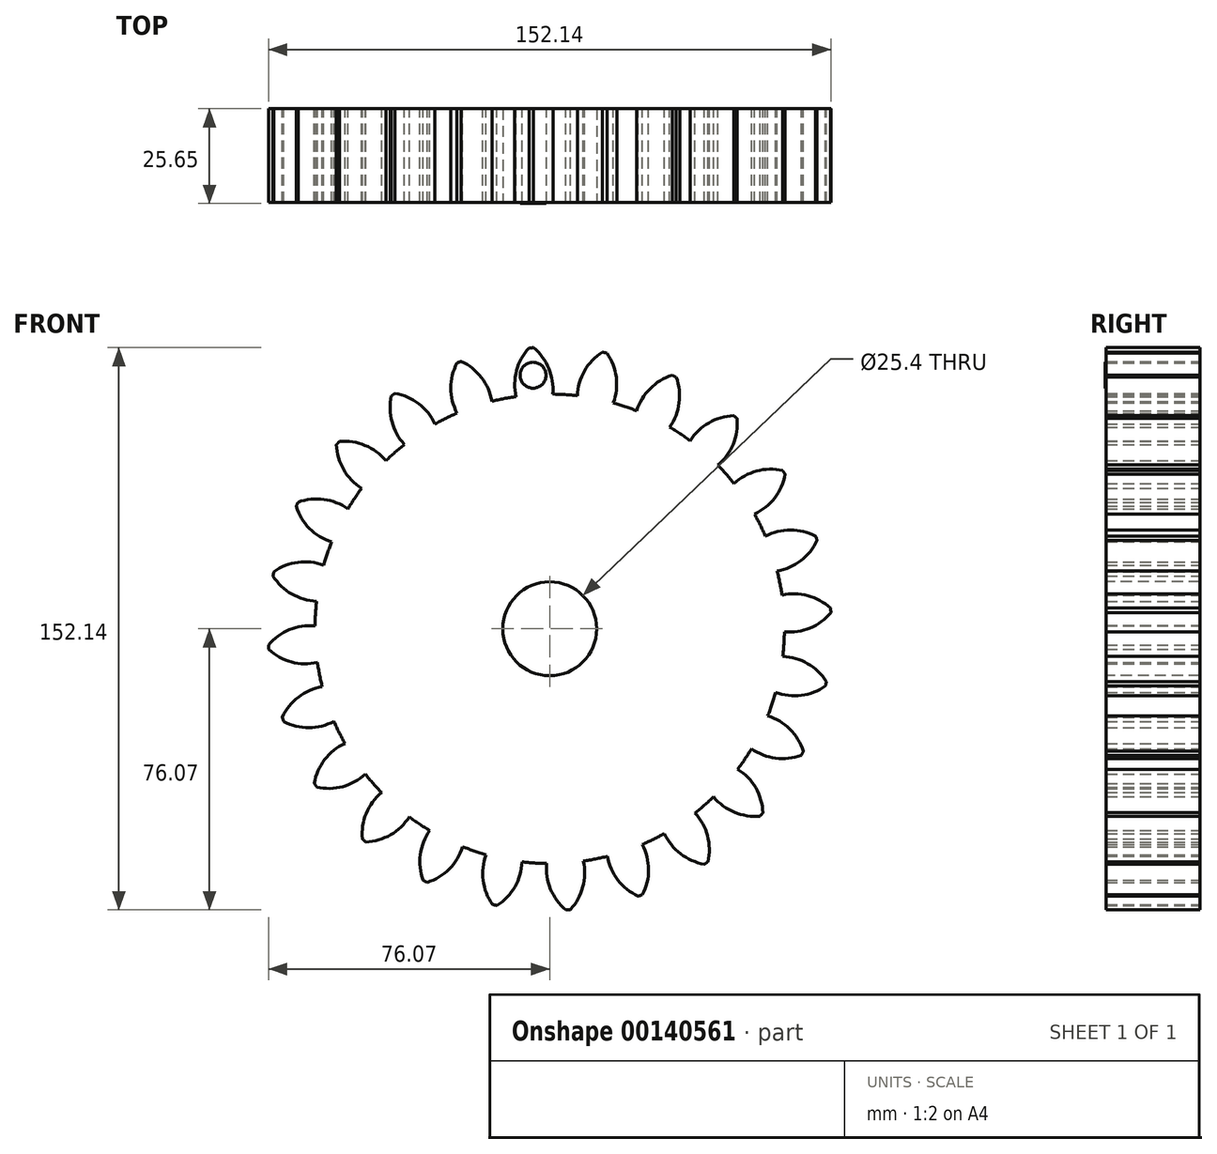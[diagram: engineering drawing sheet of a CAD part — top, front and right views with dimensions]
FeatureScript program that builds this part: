
annotation { "Feature Type Name" : "Feature", "Feature Type Description" : "" }
export const myFeature = defineFeature(function(context is Context, id is Id, definition is map)
    precondition{}
    {
        {
            var Q0;
            Q0=qCreatedBy(makeId("Front.planeOp"),FACE);
            var sketch = newSketch(context, id + "F0", { "sketchPlane" : qUnion([Q0])});
            skPoint(sketch, "E0.rect.middle", {"position": v(0, 0) * mm});
            skLineSegment(sketch, "E1", {"start": v(0, 0) * mm, "end": v(0, 76.2) * mm});
            skLineSegment(sketch, "E2", {"start": v(0, 0) * mm, "end": v(0, -76.2) * mm});
            skLineSegment(sketch, "E3", {"start": v(0, 0) * mm, "end": v(19.72, 73.6) * mm});
            skLineSegment(sketch, "E4", {"start": v(0, 0) * mm, "end": v(38.1, 66) * mm});
            skLineSegment(sketch, "E5", {"start": v(0, 0) * mm, "end": v(53.88, 53.88) * mm});
            skLineSegment(sketch, "E6", {"start": v(0, 0) * mm, "end": v(66, 38.1) * mm});
            skLineSegment(sketch, "E7", {"start": v(0, 0) * mm, "end": v(73.6, 19.72) * mm});
            skLineSegment(sketch, "E8", {"start": v(0, 0) * mm, "end": v(76.2, 0) * mm});
            skLineSegment(sketch, "E9", {"start": v(0, 0) * mm, "end": v(73.6, -19.72) * mm});
            skLineSegment(sketch, "E10", {"start": v(0, 0) * mm, "end": v(66, -38.1) * mm});
            skLineSegment(sketch, "E11", {"start": v(0, 0) * mm, "end": v(53.88, -53.88) * mm});
            skLineSegment(sketch, "E12", {"start": v(0, 0) * mm, "end": v(38.1, -66) * mm});
            skLineSegment(sketch, "E13", {"start": v(0, 0) * mm, "end": v(19.72, -73.6) * mm});
            skLineSegment(sketch, "E14", {"start": v(0, 0) * mm, "end": v(-19.72, -73.6) * mm});
            skLineSegment(sketch, "E15", {"start": v(0, 0) * mm, "end": v(-38.1, -66) * mm});
            skLineSegment(sketch, "E16", {"start": v(0, 0) * mm, "end": v(-53.88, -53.88) * mm});
            skLineSegment(sketch, "E17", {"start": v(0, 0) * mm, "end": v(-66, -38.1) * mm});
            skLineSegment(sketch, "E18", {"start": v(0, 0) * mm, "end": v(-73.6, -19.72) * mm});
            skLineSegment(sketch, "E19", {"start": v(0, 0) * mm, "end": v(-76.2, 0.07) * mm});
            skLineSegment(sketch, "E20", {"start": v(0, 0) * mm, "end": v(-73.6, 19.72) * mm});
            skLineSegment(sketch, "E21", {"start": v(0, 0) * mm, "end": v(-66, 38.1) * mm});
            skLineSegment(sketch, "E22", {"start": v(0, 0) * mm, "end": v(-53.88, 53.88) * mm});
            skLineSegment(sketch, "E23", {"start": v(0, 0) * mm, "end": v(-38.1, 66) * mm});
            skLineSegment(sketch, "E24", {"start": v(0, 0) * mm, "end": v(-19.72, 73.6) * mm});
            skCircle(sketch, "E25", {"center": v(0, 0) * mm, "radius": 76.2 * mm});
            skCircle(sketch, "E26", {"center": v(0, 0) * mm, "radius": 69.85 * mm});
            skCircle(sketch, "E27", {"center": v(0, 0) * mm, "radius": 63.5 * mm});
            skLineSegment(sketch, "E28", {"start": v(0, 0) * mm, "end": v(-4.98, 76.04) * mm});
            skLineSegment(sketch, "E29", {"start": v(0, 69.85) * mm, "end": v(-76.58, 69.85) * mm});
            skLineSegment(sketch, "E30", {"start": v(0, 69.85) * mm, "end": v(-76.5, 42) * mm});
            skLineSegment(sketch, "E31", {"start": v(-4.98, 76.04) * mm, "end": v(-7.15, 109.16) * mm});
            skLineSegment(sketch, "E32", {"start": v(0, 76.2) * mm, "end": v(0, 110.22) * mm});
            skCircle(sketch, "E33", {"center": v(0, 69.85) * mm, "radius": 14.6 * mm});
            skPoint(sketch, "E34", {"position": v(-13.72, 64.85) * mm});
            skArc(sketch, "E35", {"start": v(0.82, 63.5) * mm, "mid": v(-0.22, 70.43) * mm, "end": v(-4.37, 76.07) * mm});
            skArc(sketch, "E36.MirrorCS", {"start": v(-9.1, 62.84) * mm, "mid": v(-8.97, 69.85) * mm, "end": v(-5.6, 76) * mm});
            skSolve(sketch);
        }
        {
            var Q0;
            {var subQ1=sQuery(id+"F0.wireOp",EDGE,"E23");var subQ3=sQuery(id+"F0.wireOp",EDGE,"E27");var subQ4=makeQuery(id+"F0.imprint","INTERSECT",VERTEX,{"derivedFrom":[subQ1,subQ3]});Q0=makeQuery(id+"F0.imprint","IMPRINT",FACE,{"disambiguationData":[TD([[makeQuery(id+"F0.imprint","IMPRINT",EDGE,{"disambiguationData":[TD([[subQ4,1.0]])],"derivedFrom":subQ3}),1.0]])]});}
            var Q1;
            {var subQ1=sQuery(id+"F0.wireOp",EDGE,"E22");var subQ3=sQuery(id+"F0.wireOp",EDGE,"E27");var subQ4=makeQuery(id+"F0.imprint","INTERSECT",VERTEX,{"derivedFrom":[subQ1,subQ3]});Q1=makeQuery(id+"F0.imprint","IMPRINT",FACE,{"disambiguationData":[TD([[makeQuery(id+"F0.imprint","IMPRINT",EDGE,{"disambiguationData":[TD([[subQ4,1.0]])],"derivedFrom":subQ3}),1.0]])]});}
            var Q2;
            {var subQ1=sQuery(id+"F0.wireOp",EDGE,"E1");var subQ3=sQuery(id+"F0.wireOp",EDGE,"E33");var subQ4=makeQuery(id+"F0.imprint","INTERSECT",VERTEX,{"derivedFrom":[subQ1,subQ3]});Q2=makeQuery(id+"F0.imprint","IMPRINT",FACE,{"disambiguationData":[TD([[makeQuery(id+"F0.imprint","IMPRINT",EDGE,{"disambiguationData":[TD([[subQ4,1.0]])],"derivedFrom":subQ3}),-1.0]])]});}
            var Q3;
            {var subQ1=sQuery(id+"F0.wireOp",EDGE,"E19");var subQ3=sQuery(id+"F0.wireOp",EDGE,"E27");var subQ4=makeQuery(id+"F0.imprint","INTERSECT",VERTEX,{"derivedFrom":[subQ1,subQ3]});Q3=makeQuery(id+"F0.imprint","IMPRINT",FACE,{"disambiguationData":[TD([[makeQuery(id+"F0.imprint","IMPRINT",EDGE,{"disambiguationData":[TD([[subQ4,1.0]])],"derivedFrom":subQ3}),1.0]])]});}
            var Q4;
            {var subQ1=sQuery(id+"F0.wireOp",EDGE,"E24");var subQ3=sQuery(id+"F0.wireOp",EDGE,"E27");var subQ4=makeQuery(id+"F0.imprint","INTERSECT",VERTEX,{"derivedFrom":[subQ1,subQ3]});Q4=makeQuery(id+"F0.imprint","IMPRINT",FACE,{"disambiguationData":[TD([[makeQuery(id+"F0.imprint","IMPRINT",EDGE,{"disambiguationData":[TD([[subQ4,1.0]])],"derivedFrom":subQ3}),1.0]])]});}
            var Q5;
            {var subQ1=sQuery(id+"F0.wireOp",EDGE,"E20");var subQ3=sQuery(id+"F0.wireOp",EDGE,"E27");var subQ4=makeQuery(id+"F0.imprint","INTERSECT",VERTEX,{"derivedFrom":[subQ1,subQ3]});Q5=makeQuery(id+"F0.imprint","IMPRINT",FACE,{"disambiguationData":[TD([[makeQuery(id+"F0.imprint","IMPRINT",EDGE,{"disambiguationData":[TD([[subQ4,1.0]])],"derivedFrom":subQ3}),1.0]])]});}
            var Q6;
            {var subQ1=sQuery(id+"F0.wireOp",EDGE,"E21");var subQ3=sQuery(id+"F0.wireOp",EDGE,"E27");var subQ4=makeQuery(id+"F0.imprint","INTERSECT",VERTEX,{"derivedFrom":[subQ1,subQ3]});Q6=makeQuery(id+"F0.imprint","IMPRINT",FACE,{"disambiguationData":[TD([[makeQuery(id+"F0.imprint","IMPRINT",EDGE,{"disambiguationData":[TD([[subQ4,1.0]])],"derivedFrom":subQ3}),1.0]])]});}
            var Q7;
            {var subQ1=sQuery(id+"F0.wireOp",EDGE,"E6");var subQ3=sQuery(id+"F0.wireOp",EDGE,"E27");var subQ4=makeQuery(id+"F0.imprint","INTERSECT",VERTEX,{"derivedFrom":[subQ1,subQ3]});Q7=makeQuery(id+"F0.imprint","IMPRINT",FACE,{"disambiguationData":[TD([[makeQuery(id+"F0.imprint","IMPRINT",EDGE,{"disambiguationData":[TD([[subQ4,1.0]])],"derivedFrom":subQ3}),1.0]])]});}
            var Q8;
            {var subQ1=sQuery(id+"F0.wireOp",EDGE,"E4");var subQ3=sQuery(id+"F0.wireOp",EDGE,"E27");var subQ4=makeQuery(id+"F0.imprint","INTERSECT",VERTEX,{"derivedFrom":[subQ1,subQ3]});Q8=makeQuery(id+"F0.imprint","IMPRINT",FACE,{"disambiguationData":[TD([[makeQuery(id+"F0.imprint","IMPRINT",EDGE,{"disambiguationData":[TD([[subQ4,1.0]])],"derivedFrom":subQ3}),1.0]])]});}
            var Q9;
            {var subQ1=sQuery(id+"F0.wireOp",EDGE,"E7");var subQ3=sQuery(id+"F0.wireOp",EDGE,"E27");var subQ4=makeQuery(id+"F0.imprint","INTERSECT",VERTEX,{"derivedFrom":[subQ1,subQ3]});Q9=makeQuery(id+"F0.imprint","IMPRINT",FACE,{"disambiguationData":[TD([[makeQuery(id+"F0.imprint","IMPRINT",EDGE,{"disambiguationData":[TD([[subQ4,1.0]])],"derivedFrom":subQ3}),1.0]])]});}
            var Q10;
            {var subQ0=sQuery(id+"F0.wireOp",EDGE,"E3");var subQ5=sQuery(id+"F0.wireOp",EDGE,"E27");var subQ6=makeQuery(id+"F0.imprint","INTERSECT",VERTEX,{"derivedFrom":[subQ0,subQ5]});Q10=makeQuery(id+"F0.imprint","IMPRINT",FACE,{"disambiguationData":[TD([[makeQuery(id+"F0.imprint","IMPRINT",EDGE,{"disambiguationData":[TD([[subQ6,-1.0]])],"derivedFrom":subQ5}),1.0]])]});}
            var Q11;
            {var subQ1=sQuery(id+"F0.wireOp",EDGE,"E3");var subQ3=sQuery(id+"F0.wireOp",EDGE,"E27");var subQ4=makeQuery(id+"F0.imprint","INTERSECT",VERTEX,{"derivedFrom":[subQ1,subQ3]});Q11=makeQuery(id+"F0.imprint","IMPRINT",FACE,{"disambiguationData":[TD([[makeQuery(id+"F0.imprint","IMPRINT",EDGE,{"disambiguationData":[TD([[subQ4,1.0]])],"derivedFrom":subQ3}),1.0]])]});}
            var Q12;
            {var subQ1=sQuery(id+"F0.wireOp",EDGE,"E5");var subQ3=sQuery(id+"F0.wireOp",EDGE,"E27");var subQ4=makeQuery(id+"F0.imprint","INTERSECT",VERTEX,{"derivedFrom":[subQ1,subQ3]});Q12=makeQuery(id+"F0.imprint","IMPRINT",FACE,{"disambiguationData":[TD([[makeQuery(id+"F0.imprint","IMPRINT",EDGE,{"disambiguationData":[TD([[subQ4,1.0]])],"derivedFrom":subQ3}),1.0]])]});}
            var Q13;
            {var subQ1=sQuery(id+"F0.wireOp",EDGE,"E17");var subQ3=sQuery(id+"F0.wireOp",EDGE,"E27");var subQ4=makeQuery(id+"F0.imprint","INTERSECT",VERTEX,{"derivedFrom":[subQ1,subQ3]});Q13=makeQuery(id+"F0.imprint","IMPRINT",FACE,{"disambiguationData":[TD([[makeQuery(id+"F0.imprint","IMPRINT",EDGE,{"disambiguationData":[TD([[subQ4,1.0]])],"derivedFrom":subQ3}),1.0]])]});}
            var Q14;
            {var subQ1=sQuery(id+"F0.wireOp",EDGE,"E15");var subQ3=sQuery(id+"F0.wireOp",EDGE,"E27");var subQ4=makeQuery(id+"F0.imprint","INTERSECT",VERTEX,{"derivedFrom":[subQ1,subQ3]});Q14=makeQuery(id+"F0.imprint","IMPRINT",FACE,{"disambiguationData":[TD([[makeQuery(id+"F0.imprint","IMPRINT",EDGE,{"disambiguationData":[TD([[subQ4,1.0]])],"derivedFrom":subQ3}),1.0]])]});}
            var Q15;
            {var subQ1=sQuery(id+"F0.wireOp",EDGE,"E16");var subQ3=sQuery(id+"F0.wireOp",EDGE,"E27");var subQ4=makeQuery(id+"F0.imprint","INTERSECT",VERTEX,{"derivedFrom":[subQ1,subQ3]});Q15=makeQuery(id+"F0.imprint","IMPRINT",FACE,{"disambiguationData":[TD([[makeQuery(id+"F0.imprint","IMPRINT",EDGE,{"disambiguationData":[TD([[subQ4,1.0]])],"derivedFrom":subQ3}),1.0]])]});}
            var Q16;
            {var subQ1=sQuery(id+"F0.wireOp",EDGE,"E2");var subQ3=sQuery(id+"F0.wireOp",EDGE,"E27");var subQ4=makeQuery(id+"F0.imprint","INTERSECT",VERTEX,{"derivedFrom":[subQ1,subQ3]});Q16=makeQuery(id+"F0.imprint","IMPRINT",FACE,{"disambiguationData":[TD([[makeQuery(id+"F0.imprint","IMPRINT",EDGE,{"disambiguationData":[TD([[subQ4,1.0]])],"derivedFrom":subQ3}),1.0]])]});}
            var Q17;
            {var subQ1=sQuery(id+"F0.wireOp",EDGE,"E14");var subQ3=sQuery(id+"F0.wireOp",EDGE,"E27");var subQ4=makeQuery(id+"F0.imprint","INTERSECT",VERTEX,{"derivedFrom":[subQ1,subQ3]});Q17=makeQuery(id+"F0.imprint","IMPRINT",FACE,{"disambiguationData":[TD([[makeQuery(id+"F0.imprint","IMPRINT",EDGE,{"disambiguationData":[TD([[subQ4,1.0]])],"derivedFrom":subQ3}),1.0]])]});}
            var Q18;
            {var subQ1=sQuery(id+"F0.wireOp",EDGE,"E18");var subQ3=sQuery(id+"F0.wireOp",EDGE,"E27");var subQ4=makeQuery(id+"F0.imprint","INTERSECT",VERTEX,{"derivedFrom":[subQ1,subQ3]});Q18=makeQuery(id+"F0.imprint","IMPRINT",FACE,{"disambiguationData":[TD([[makeQuery(id+"F0.imprint","IMPRINT",EDGE,{"disambiguationData":[TD([[subQ4,1.0]])],"derivedFrom":subQ3}),1.0]])]});}
            var Q19;
            {var subQ0=sQuery(id+"F0.wireOp",EDGE,"E33");var subQ1=sQuery(id+"F0.wireOp",EDGE,"E1");var subQ2=makeQuery(id+"F0.imprint","INTERSECT",VERTEX,{"derivedFrom":[subQ1,subQ0]});Q19=makeQuery(id+"F0.imprint","IMPRINT",FACE,{"disambiguationData":[TD([[makeQuery(id+"F0.imprint","IMPRINT",EDGE,{"disambiguationData":[TD([[subQ2,-1.0]])],"derivedFrom":subQ1}),1.0]])]});}
            var Q20;
            {var subQ0=sQuery(id+"F0.wireOp",EDGE,"E27");var subQ1=makeQuery(id+"F0.imprint","INTERSECT",VERTEX,{"derivedFrom":[subQ0,sQuery(id+"F0.wireOp",EDGE,"E36.MirrorCS")]});Q20=makeQuery(id+"F0.imprint","IMPRINT",FACE,{"disambiguationData":[TD([[makeQuery(id+"F0.imprint","IMPRINT",EDGE,{"disambiguationData":[TD([[subQ1,1.0]])],"derivedFrom":subQ0}),1.0]])]});}
            var Q21;
            {var subQ0=sQuery(id+"F0.wireOp",EDGE,"E33");var subQ1=sQuery(id+"F0.wireOp",EDGE,"E1");var subQ2=makeQuery(id+"F0.imprint","INTERSECT",VERTEX,{"derivedFrom":[subQ1,subQ0]});Q21=makeQuery(id+"F0.imprint","IMPRINT",FACE,{"disambiguationData":[TD([[makeQuery(id+"F0.imprint","IMPRINT",EDGE,{"disambiguationData":[TD([[subQ2,-1.0]])],"derivedFrom":subQ1}),-1.0]])]});}
            var Q22;
            {var subQ1=sQuery(id+"F0.wireOp",EDGE,"E1");var subQ3=sQuery(id+"F0.wireOp",EDGE,"E27");var subQ4=makeQuery(id+"F0.imprint","INTERSECT",VERTEX,{"derivedFrom":[subQ1,subQ3]});Q22=makeQuery(id+"F0.imprint","IMPRINT",FACE,{"disambiguationData":[TD([[makeQuery(id+"F0.imprint","IMPRINT",EDGE,{"disambiguationData":[TD([[subQ4,-1.0]])],"derivedFrom":subQ3}),-1.0]])]});}
            var Q23;
            {var subQ0=sQuery(id+"F0.wireOp",EDGE,"E36.MirrorCS");var subQ1=sQuery(id+"F0.wireOp",EDGE,"E27");var subQ2=makeQuery(id+"F0.imprint","INTERSECT",VERTEX,{"derivedFrom":[subQ1,subQ0]});Q23=makeQuery(id+"F0.imprint","IMPRINT",FACE,{"disambiguationData":[TD([[makeQuery(id+"F0.imprint","IMPRINT",EDGE,{"disambiguationData":[TD([[subQ2,1.0]])],"derivedFrom":subQ1}),-1.0]])]});}
            var Q24;
            {var subQ0=sQuery(id+"F0.wireOp",EDGE,"E28");var subQ1=sQuery(id+"F0.wireOp",EDGE,"E26");var subQ2=makeQuery(id+"F0.imprint","INTERSECT",VERTEX,{"derivedFrom":[subQ1,subQ0]});Q24=makeQuery(id+"F0.imprint","IMPRINT",FACE,{"disambiguationData":[TD([[makeQuery(id+"F0.imprint","IMPRINT",EDGE,{"disambiguationData":[TD([[subQ2,-1.0]])],"derivedFrom":subQ1}),1.0]])]});}
            var Q25;
            {var subQ0=sQuery(id+"F0.wireOp",EDGE,"E28");var subQ1=sQuery(id+"F0.wireOp",EDGE,"E26");var subQ2=makeQuery(id+"F0.imprint","INTERSECT",VERTEX,{"derivedFrom":[subQ1,subQ0]});Q25=makeQuery(id+"F0.imprint","IMPRINT",FACE,{"disambiguationData":[TD([[makeQuery(id+"F0.imprint","IMPRINT",EDGE,{"disambiguationData":[TD([[subQ2,-1.0]])],"derivedFrom":subQ1}),-1.0]])]});}
            var Q26;
            {var subQ0=sQuery(id+"F0.wireOp",EDGE,"E28");var subQ5=sQuery(id+"F0.wireOp",EDGE,"E29");var subQ6=makeQuery(id+"F0.imprint","INTERSECT",VERTEX,{"derivedFrom":[subQ0,subQ5]});Q26=makeQuery(id+"F0.imprint","IMPRINT",FACE,{"disambiguationData":[TD([[makeQuery(id+"F0.imprint","IMPRINT",EDGE,{"disambiguationData":[TD([[subQ6,-1.0]])],"derivedFrom":subQ5}),-1.0]])]});}
            var Q27;
            {var subQ1=sQuery(id+"F0.wireOp",EDGE,"E25");var subQ3=sQuery(id+"F0.wireOp",EDGE,"E35");var subQ4=makeQuery(id+"F0.imprint","INTERSECT",VERTEX,{"derivedFrom":[subQ1,subQ3]});Q27=makeQuery(id+"F0.imprint","IMPRINT",FACE,{"disambiguationData":[TD([[makeQuery(id+"F0.imprint","IMPRINT",EDGE,{"disambiguationData":[TD([[subQ4,-1.0]])],"derivedFrom":subQ1}),1.0]])]});}
            var Q28;
            {var subQ0=sQuery(id+"F0.wireOp",EDGE,"E35");var subQ3=sQuery(id+"F0.wireOp",EDGE,"E27");var subQ5=makeQuery(id+"F0.imprint","INTERSECT",VERTEX,{"derivedFrom":[subQ3,subQ0]});Q28=makeQuery(id+"F0.imprint","IMPRINT",FACE,{"disambiguationData":[TD([[makeQuery(id+"F0.imprint","IMPRINT",EDGE,{"disambiguationData":[TD([[subQ5,-1.0]])],"derivedFrom":subQ3}),-1.0]])]});}
            var Q29;
            {var subQ1=sQuery(id+"F0.wireOp",EDGE,"E26");var subQ3=sQuery(id+"F0.wireOp",EDGE,"E28");var subQ4=makeQuery(id+"F0.imprint","INTERSECT",VERTEX,{"derivedFrom":[subQ1,subQ3]});Q29=makeQuery(id+"F0.imprint","IMPRINT",FACE,{"disambiguationData":[TD([[makeQuery(id+"F0.imprint","IMPRINT",EDGE,{"disambiguationData":[TD([[subQ4,-1.0]])],"derivedFrom":subQ3}),-1.0]])]});}
            var Q30;
            {var subQ1=sQuery(id+"F0.wireOp",EDGE,"E26");var subQ3=sQuery(id+"F0.wireOp",EDGE,"E28");var subQ4=makeQuery(id+"F0.imprint","INTERSECT",VERTEX,{"derivedFrom":[subQ1,subQ3]});Q30=makeQuery(id+"F0.imprint","IMPRINT",FACE,{"disambiguationData":[TD([[makeQuery(id+"F0.imprint","IMPRINT",EDGE,{"disambiguationData":[TD([[subQ4,1.0]])],"derivedFrom":subQ3}),-1.0]])]});}
            var Q31;
            {var subQ1=sQuery(id+"F0.wireOp",EDGE,"E10");var subQ3=sQuery(id+"F0.wireOp",EDGE,"E27");var subQ4=makeQuery(id+"F0.imprint","INTERSECT",VERTEX,{"derivedFrom":[subQ1,subQ3]});Q31=makeQuery(id+"F0.imprint","IMPRINT",FACE,{"disambiguationData":[TD([[makeQuery(id+"F0.imprint","IMPRINT",EDGE,{"disambiguationData":[TD([[subQ4,1.0]])],"derivedFrom":subQ3}),1.0]])]});}
            var Q32;
            {var subQ1=sQuery(id+"F0.wireOp",EDGE,"E9");var subQ3=sQuery(id+"F0.wireOp",EDGE,"E27");var subQ4=makeQuery(id+"F0.imprint","INTERSECT",VERTEX,{"derivedFrom":[subQ1,subQ3]});Q32=makeQuery(id+"F0.imprint","IMPRINT",FACE,{"disambiguationData":[TD([[makeQuery(id+"F0.imprint","IMPRINT",EDGE,{"disambiguationData":[TD([[subQ4,1.0]])],"derivedFrom":subQ3}),1.0]])]});}
            var Q33;
            {var subQ1=sQuery(id+"F0.wireOp",EDGE,"E8");var subQ3=sQuery(id+"F0.wireOp",EDGE,"E27");var subQ4=makeQuery(id+"F0.imprint","INTERSECT",VERTEX,{"derivedFrom":[subQ1,subQ3]});Q33=makeQuery(id+"F0.imprint","IMPRINT",FACE,{"disambiguationData":[TD([[makeQuery(id+"F0.imprint","IMPRINT",EDGE,{"disambiguationData":[TD([[subQ4,1.0]])],"derivedFrom":subQ3}),1.0]])]});}
            var Q34;
            {var subQ1=sQuery(id+"F0.wireOp",EDGE,"E11");var subQ3=sQuery(id+"F0.wireOp",EDGE,"E27");var subQ4=makeQuery(id+"F0.imprint","INTERSECT",VERTEX,{"derivedFrom":[subQ1,subQ3]});Q34=makeQuery(id+"F0.imprint","IMPRINT",FACE,{"disambiguationData":[TD([[makeQuery(id+"F0.imprint","IMPRINT",EDGE,{"disambiguationData":[TD([[subQ4,1.0]])],"derivedFrom":subQ3}),1.0]])]});}
            var Q35;
            {var subQ1=sQuery(id+"F0.wireOp",EDGE,"E2");var subQ3=sQuery(id+"F0.wireOp",EDGE,"E27");var subQ4=makeQuery(id+"F0.imprint","INTERSECT",VERTEX,{"derivedFrom":[subQ1,subQ3]});Q35=makeQuery(id+"F0.imprint","IMPRINT",FACE,{"disambiguationData":[TD([[makeQuery(id+"F0.imprint","IMPRINT",EDGE,{"disambiguationData":[TD([[subQ4,-1.0]])],"derivedFrom":subQ3}),1.0]])]});}
            var Q36;
            {var subQ1=sQuery(id+"F0.wireOp",EDGE,"E12");var subQ3=sQuery(id+"F0.wireOp",EDGE,"E27");var subQ4=makeQuery(id+"F0.imprint","INTERSECT",VERTEX,{"derivedFrom":[subQ1,subQ3]});Q36=makeQuery(id+"F0.imprint","IMPRINT",FACE,{"disambiguationData":[TD([[makeQuery(id+"F0.imprint","IMPRINT",EDGE,{"disambiguationData":[TD([[subQ4,1.0]])],"derivedFrom":subQ3}),1.0]])]});}
            extrude(context, id + "F1", {"entities" : qUnion([Q0, Q1, Q2, Q3, Q4, Q5, Q6, Q7, Q8, Q9, Q10, Q11, Q12, Q13, Q14, Q15, Q16, Q17, Q18, Q19, Q20, Q21, Q22, Q23, Q24, Q25, Q26, Q27, Q28, Q29, Q30, Q31, Q32, Q33, Q34, Q35, Q36]), "endBound" : BoundingType.SYMMETRIC, "depth" : 25.4 * mm});
        }
        {
            var Q0;
            Q0=makeQuery(id+"F1.opExtrude","SWEPT_BODY",BODY,{"disambiguationData":[OSD([sQuery(id+"F0.wireOp",EDGE,"E25"),sQuery(id+"F0.wireOp",EDGE,"E27"),sQuery(id+"F0.wireOp",EDGE,"E35"),sQuery(id+"F0.wireOp",EDGE,"E36.MirrorCS")])]});
            var Q1;
            Q1=makeQuery(id+"F1.opExtrude","SWEPT_FACE",FACE,{"disambiguationData":[OSD([sQuery(id+"F0.wireOp",EDGE,"E27")])]});
            circularPattern(context, id + "F2", {"operationType" : NewBodyOperationType.ADD, "entities" : qUnion([Q0]), "axis" : qUnion([Q1]), "angle" : 15 * degree, "instanceCount" : 24});
        }
        {
            var Q0;
            Q0=makeQuery(id+"F1.opExtrude","CAP_FACE",FACE,{"disambiguationData":[OSD([sQuery(id+"F0.wireOp",EDGE,"E25"),sQuery(id+"F0.wireOp",EDGE,"E27"),sQuery(id+"F0.wireOp",EDGE,"E35"),sQuery(id+"F0.wireOp",EDGE,"E36.MirrorCS")])],"isStart":false});
            var sketch = newSketch(context, id + "F3", { "sketchPlane" : qUnion([Q0])});
            skPoint(sketch, "E37", {"position": v(0, 0) * mm});
            skSolve(sketch);
        }
        {
            var Q0;
            Q0=sQuery(id+"F3.wireOp",VERTEX,"E37");
            var Q1;
            Q1=makeQuery(id+"F1.opExtrude","SWEPT_BODY",BODY,{"disambiguationData":[OSD([sQuery(id+"F0.wireOp",EDGE,"E25"),sQuery(id+"F0.wireOp",EDGE,"E27"),sQuery(id+"F0.wireOp",EDGE,"E35"),sQuery(id+"F0.wireOp",EDGE,"E36.MirrorCS")])]});
            hole(context, id + "F4", {"style" : HoleStyle.SIMPLE, "holeDiameter" : 25.4 * mm, "endStyle" : HoleEndStyle.THROUGH, "locations" : qUnion([Q0]), "scope" : qUnion([Q1])});
        }
        {
            var Q0;
            {var subQ0=makeQuery(id+"F1.opExtrude","CAP_FACE",FACE,{"disambiguationData":[OSD([sQuery(id+"F0.wireOp",EDGE,"E25"),sQuery(id+"F0.wireOp",EDGE,"E27"),sQuery(id+"F0.wireOp",EDGE,"E35"),sQuery(id+"F0.wireOp",EDGE,"E36.MirrorCS")])],"isStart":false});Q0=makeQuery(id+"F2.boolean.opBoolean","MERGE",FACE,{"derivedFrom":[subQ0,makeQuery(id+"F2.opPattern","COPY",FACE,{"derivedFrom":subQ0,"instanceName":"1"}),makeQuery(id+"F2.opPattern","COPY",FACE,{"derivedFrom":subQ0,"instanceName":"2"}),makeQuery(id+"F2.opPattern","COPY",FACE,{"derivedFrom":subQ0,"instanceName":"3"}),makeQuery(id+"F2.opPattern","COPY",FACE,{"derivedFrom":subQ0,"instanceName":"4"}),makeQuery(id+"F2.opPattern","COPY",FACE,{"derivedFrom":subQ0,"instanceName":"5"}),makeQuery(id+"F2.opPattern","COPY",FACE,{"derivedFrom":subQ0,"instanceName":"6"}),makeQuery(id+"F2.opPattern","COPY",FACE,{"derivedFrom":subQ0,"instanceName":"7"}),makeQuery(id+"F2.opPattern","COPY",FACE,{"derivedFrom":subQ0,"instanceName":"8"}),makeQuery(id+"F2.opPattern","COPY",FACE,{"derivedFrom":subQ0,"instanceName":"9"}),makeQuery(id+"F2.opPattern","COPY",FACE,{"derivedFrom":subQ0,"instanceName":"10"}),makeQuery(id+"F2.opPattern","COPY",FACE,{"derivedFrom":subQ0,"instanceName":"11"}),makeQuery(id+"F2.opPattern","COPY",FACE,{"derivedFrom":subQ0,"instanceName":"12"}),makeQuery(id+"F2.opPattern","COPY",FACE,{"derivedFrom":subQ0,"instanceName":"13"}),makeQuery(id+"F2.opPattern","COPY",FACE,{"derivedFrom":subQ0,"instanceName":"14"}),makeQuery(id+"F2.opPattern","COPY",FACE,{"derivedFrom":subQ0,"instanceName":"15"}),makeQuery(id+"F2.opPattern","COPY",FACE,{"derivedFrom":subQ0,"instanceName":"16"}),makeQuery(id+"F2.opPattern","COPY",FACE,{"derivedFrom":subQ0,"instanceName":"17"}),makeQuery(id+"F2.opPattern","COPY",FACE,{"derivedFrom":subQ0,"instanceName":"18"}),makeQuery(id+"F2.opPattern","COPY",FACE,{"derivedFrom":subQ0,"instanceName":"19"}),makeQuery(id+"F2.opPattern","COPY",FACE,{"derivedFrom":subQ0,"instanceName":"20"}),makeQuery(id+"F2.opPattern","COPY",FACE,{"derivedFrom":subQ0,"instanceName":"21"}),makeQuery(id+"F2.opPattern","COPY",FACE,{"derivedFrom":subQ0,"instanceName":"22"}),makeQuery(id+"F2.opPattern","COPY",FACE,{"derivedFrom":subQ0,"instanceName":"23"})]});}
            var sketch = newSketch(context, id + "F5", { "sketchPlane" : qUnion([Q0])});
            skCircle(sketch, "E38", {"center": v(-4.51, 68.62) * mm, "radius": 3.51 * mm});
            skSolve(sketch);
        }
        {
            var Q0;
            Q0=makeQuery(id+"F5.imprint","IMPRINT",FACE,{"disambiguationData":[TD([[makeQuery(id+"F5.imprint","IMPRINT",EDGE,{"derivedFrom":sQuery(id+"F5.wireOp",EDGE,"E38")}),1.0]])]});
            extrude(context, id + "F6", {"entities" : qUnion([Q0]), "operationType" : NewBodyOperationType.ADD, "depth" : 0.25 * mm});
        }
    });
